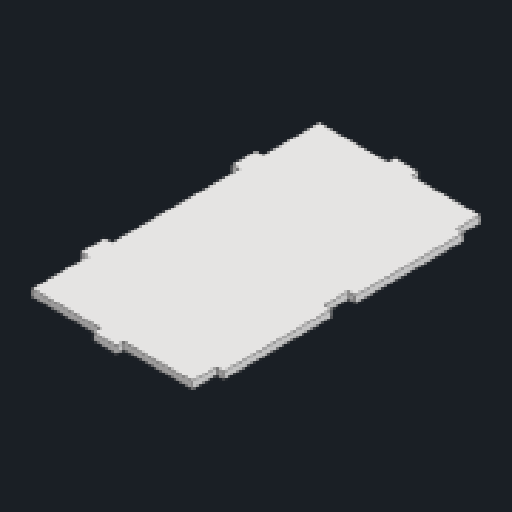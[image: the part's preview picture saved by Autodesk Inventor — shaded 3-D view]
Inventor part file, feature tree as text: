
AUTODESK INVENTOR PART (.ipt)
format: ipt  version: 2023 (Build 270158000, 158)  size: 146,432 bytes
history: native  units: mm
features: extrude x4, sketch x4
ambient origin geometry x8: Origin, YZ Plane, XZ Plane, XY Plane, X Axis, Y Axis, Z Axis, Center Point
bodies: Solid1 (feature_tree)
feature tree (8):
  extrude  "Extrusion1"  Depth=120.0mm
  extrude  "Extrusion2"  Depth=3.0mm
  extrude  "Extrusion3"  Depth=3.0mm
  extrude  "Extrusion4"  Depth=10.0mm
  sketch  "Sketch1"  dims[d0=70.0mm d1=120.0mm]
  sketch  "Sketch2"  dims[d2=3.0mm d3=0.0mm d4=3.0mm]
  sketch  "Sketch3"  dims[d5=10.0mm d6=3.0mm]
  sketch  "Sketch4"  dims[d7=10.0mm d8=10.0mm d9=0.0mm d10=0.0mm d15=10.0mm d16=3.0mm d17=10.0mm d18=3.0mm d19=3.0mm d20=0.0mm d21=10.0mm d22=10.0mm d23=3.0mm d24=10.0mm d25=3.0mm d26=10.0mm d27=126.0mm d28=31.5mm d29=31.5mm d30=3.0mm d31=0.0mm]
